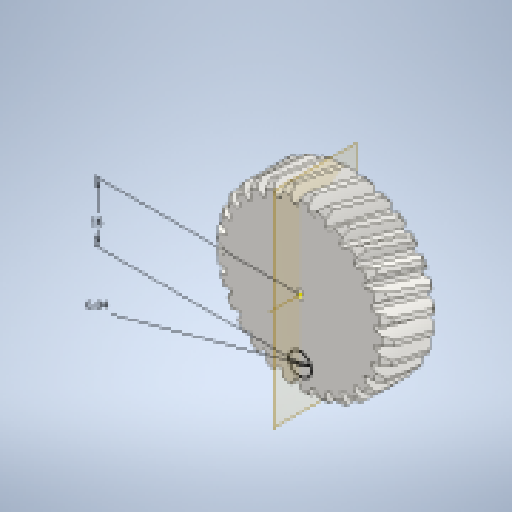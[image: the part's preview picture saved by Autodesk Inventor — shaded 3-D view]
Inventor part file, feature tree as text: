
AUTODESK INVENTOR PART (.ipt)
format: ipt  version: 2024.1 (Build 281209000, 209)  size: 803,328 bytes
history: native  units: mm (DEFAULTED — no unit token found)
features: other x4, sketch x4, extrude x3, plane x3, chamfer x2, revolve x1
ambient origin geometry x8: Origin, YZ Plane, XZ Plane, XY Plane, X Axis, Y Axis, Z Axis, Center Point
bodies: Solid1 (feature_tree)
feature tree (17):
  extrude  "Extrusion1"  Depth=14.0mm TaperAngle=0.0deg
  plane  "Work Plane2"
  plane  "Work Plane8"
  plane  "Work Plane9"
  other  "Spur Gear"
  extrude  "Extrusion2"  Depth=10.0mm TaperAngle=0.0deg
  other  "Work Axis1"
  revolve  "Revolution1"  [1 undecoded]
  extrude  "Extrusion3"  TaperAngle=0.0deg  [1 undecoded]
  chamfer  "Chamfer1"  Distance=45.0mm
  chamfer  "Chamfer2"  Distance=45.0mm
  sketch  "Sketch1"  dims[d0=47.162774mm d1=14.0mm d2=0.0mm]
  other  "Srf1"
  sketch  "Sketch3"  dims[d3=45.034514mm d4=10.0mm d5=0.0mm]
  sketch  "Sketch4"  dims[d16=45.0mm d17=0.0mm d34=1.083308mm]
  sketch  "Sketch5"  dims[d39=0.0mm d41=0.0mm d43=45.0mm d46=45.0mm d47=0.0mm d48=0.0mm d49=2.09mm d50=0.0mm d51=0.0mm d52=45.0deg d53=45.0deg d54=2.0mm d55=2.0mm d56=90.0deg d57=6.04mm d58=16.0mm d59=3.05mm d60=0.0mm d61=1.0mm d62=2.0mm d63=45.0deg d64=1.0mm d65=2.0mm d66=45.0deg]
  other  "Pitch Diameter"
note: 2 required parameter values undecoded (feature->parameter linkage not recoverable at this tier; creation-order binding heuristic only, values carry confidence <= 0.55)